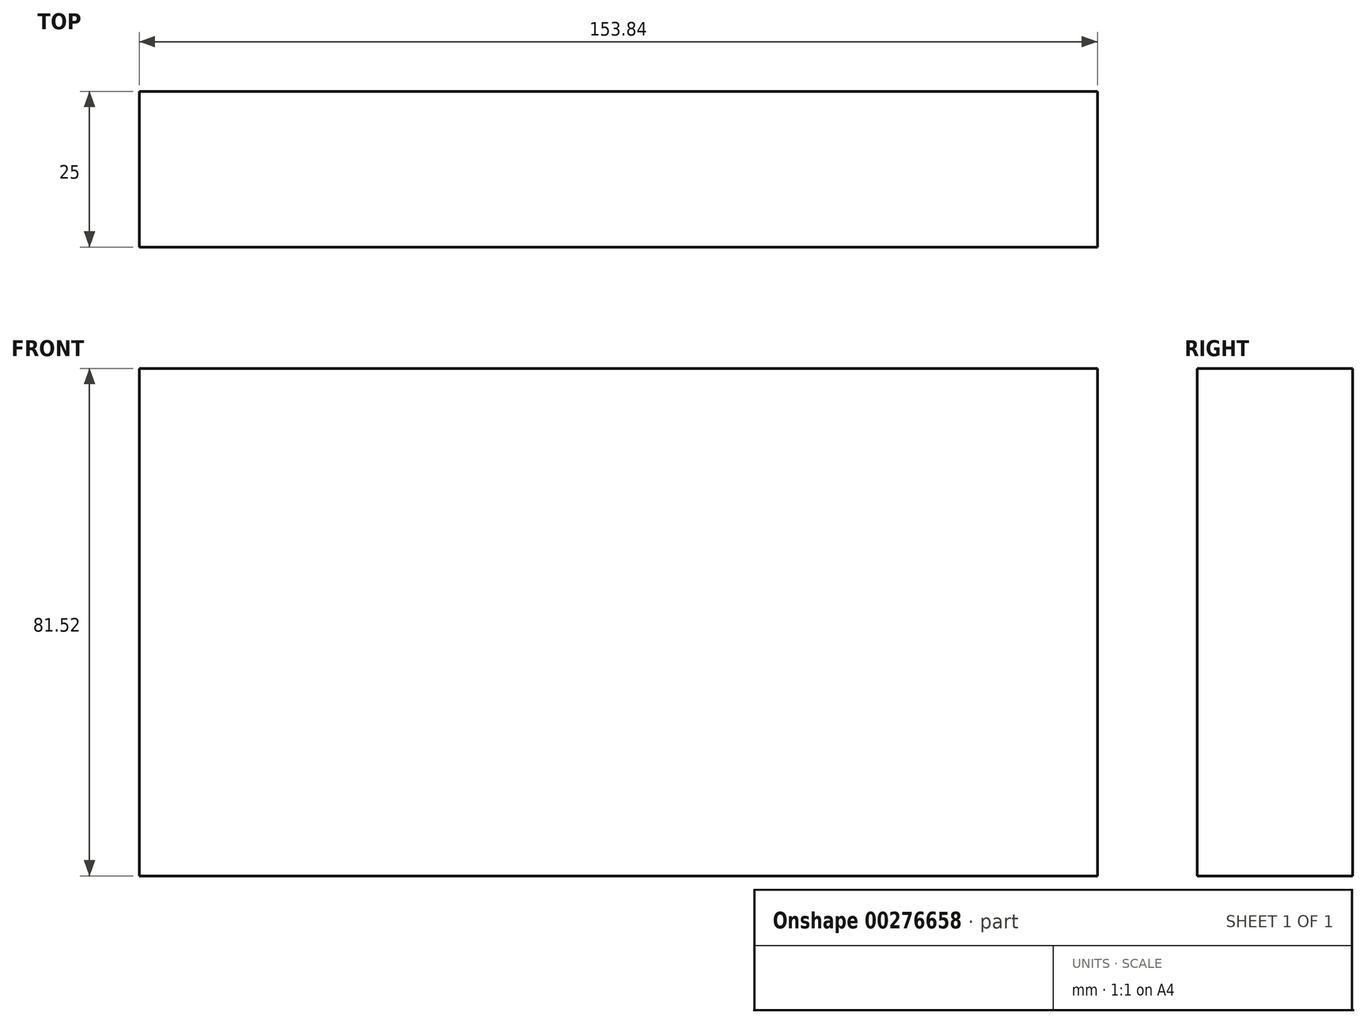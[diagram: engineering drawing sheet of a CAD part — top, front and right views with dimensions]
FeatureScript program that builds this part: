
annotation { "Feature Type Name" : "Feature", "Feature Type Description" : "" }
export const myFeature = defineFeature(function(context is Context, id is Id, definition is map)
    precondition{}
    {
        {
            var Q0;
            Q0=qCreatedBy(makeId("Front.planeOp"),FACE);
            var sketch = newSketch(context, id + "F0", { "sketchPlane" : qUnion([Q0])});
            skLineSegment(sketch, "E0.bottom", {"start": v(76.92, -40.76) * mm, "end": v(-76.92, -40.76) * mm});
            skLineSegment(sketch, "E0.top", {"start": v(76.92, 40.76) * mm, "end": v(-76.92, 40.76) * mm});
            skLineSegment(sketch, "E0.left", {"start": v(76.92, -40.76) * mm, "end": v(76.92, 40.76) * mm});
            skLineSegment(sketch, "E0.right", {"start": v(-76.92, -40.76) * mm, "end": v(-76.92, 40.76) * mm});
            skPoint(sketch, "E0.middle", {"position": v(0, 0) * mm});
            skSolve(sketch);
        }
        {
            var Q0;
            Q0 = qSketchRegion(id + "F0", true);
            extrude(context, id + "F1", {"entities" : qUnion([Q0]), "depth" : 25 * mm});
        }
    });
